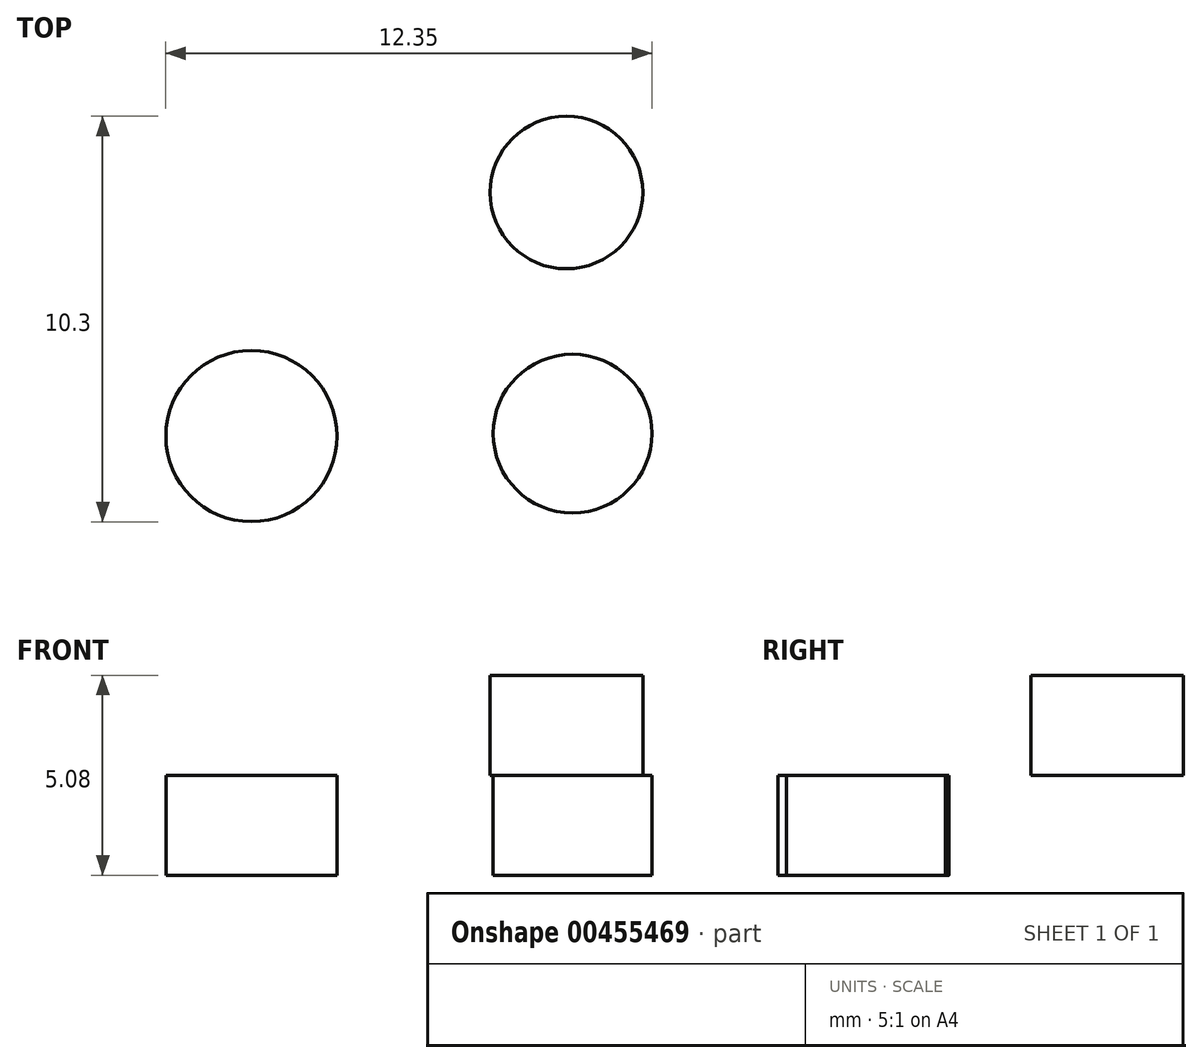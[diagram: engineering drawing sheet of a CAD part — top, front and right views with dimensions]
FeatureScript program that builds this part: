
annotation { "Feature Type Name" : "Feature", "Feature Type Description" : "" }
export const myFeature = defineFeature(function(context is Context, id is Id, definition is map)
    precondition{}
    {
        {
            var Q0;
            Q0=qCreatedBy(makeId("Top.planeOp"),FACE);
            var sketch = newSketch(context, id + "F0", { "sketchPlane" : qUnion([Q0])});
            skCircle(sketch, "E0", {"center": v(-44.55, 41.26) * mm, "radius": 2.17 * mm});
            skSolve(sketch);
        }
        {
            var Q0;
            Q0=makeQuery(id+"F0.imprint","IMPRINT",FACE,{"disambiguationData":[TD([[makeQuery(id+"F0.imprint","IMPRINT",EDGE,{"derivedFrom":sQuery(id+"F0.wireOp",EDGE,"E0")}),1.0]])]});
            var sketch = newSketch(context, id + "F1", { "sketchPlane" : qUnion([Q0])});
            skCircle(sketch, "E1", {"center": v(-36.4, 41.32) * mm, "radius": 2.02 * mm});
            skSolve(sketch);
        }
        {
            var Q0;
            Q0=qCreatedBy(makeId("Top.planeOp"),FACE);
            var sketch = newSketch(context, id + "F2", { "sketchPlane" : qUnion([Q0])});
            skCircle(sketch, "E2", {"center": v(-36.55, 47.45) * mm, "radius": 1.94 * mm});
            skSolve(sketch);
        }
        {
            var Q0;
            Q0=makeQuery(id+"F0.imprint","IMPRINT",FACE,{"disambiguationData":[TD([[makeQuery(id+"F0.imprint","IMPRINT",EDGE,{"derivedFrom":sQuery(id+"F0.wireOp",EDGE,"E0")}),1.0]])]});
            var Q1;
            Q1=makeQuery(id+"F1.imprint","IMPRINT",FACE,{"disambiguationData":[TD([[makeQuery(id+"F1.imprint","IMPRINT",EDGE,{"derivedFrom":sQuery(id+"F1.wireOp",EDGE,"E1")}),1.0]])]});
            extrude(context, id + "F3", {"entities" : qUnion([Q0, Q1]), "oppositeDirection" : true, "depth" : 2.54 * mm});
        }
        {
            var Q0;
            Q0=makeQuery(id+"F2.imprint","IMPRINT",FACE,{"disambiguationData":[TD([[makeQuery(id+"F2.imprint","IMPRINT",EDGE,{"derivedFrom":sQuery(id+"F2.wireOp",EDGE,"E2")}),1.0]])]});
            extrude(context, id + "F4", {"entities" : qUnion([Q0]), "depth" : 2.54 * mm});
        }
    });
